# Revit family: Hager-Typ.A_SP&N_DIN_Rail_Enclosures-syst-UK-en
name_source: partatom
category: Electrical Equipment
units: mm (PartAtom-declared; Revit-internal decimal feet)

## family parameters
Cut with Voids When Loaded = No
Host = Face
Panel Configuration = Two Columns, Circuits Across
Part Type = Panelboard
Room Calculation Point = No
Round Connector Dimension = Use Diameter
Shared = No

## types (8) — shared parameters
EF000003 - Mounting method = EV000384 - Surface mounted (plaster)
EF000007 - Colour = EV000154 - Other
EF000049 - Depth = 125 mm  [stored 0.410105 ft]
EF000116 - RAL-number = 7035
EF000118 - With mounting plate = No
EF000339 - Type of cover = EV004216 - Door
EF001062 - EMC-version = No
EF001088 - Extension possible = No
EF001134 - DIN-rail = No
EF001596 - Material housing = EV000179 - Steel
EF004462 - Type of closure = EV001412 - Cylinder
EF005474 - Degree of protection (IP) = EV006410 - IP30
EF006244 - Transparent cover/door = No
EF006306 - With lock = Yes
EF015776 - Earthing terminal block = Yes
EF015777 - Neutral terminal block = Yes
EF015941 - Signal passing door = No
HG000001 - Number of columns = 1
HG000002 - With door or cover = Yes
HG000003 - Range = Type A SP&N Distribution Boards
HG000005 - Thickness = 3 mm  [stored 0.00984252 ft]
HG000006 - Flush mounted = No
HG000009 - Double swing door = No
HG000010 - Asymmetric doors = No
HG000011 - Empty rows from bottom = No
HG000017 - Distance between poles = 18 mm  [stored 0.0590551 ft]
Manufacturer = Hager
Type Comments = Type A SP&N Distribution Boards
zero-valued in all types: Default Elevation, EF000218 - Built-in depth, EF000332 - Built-in height, EF000846 - Built-in width, EF001131 - Internal depth, HG000007 - Number of empty columns, HG000008 - Number of empty rows

## per-type parameters (varying)
| type | EF000008 - Width | EF000040 - Height | EF000266 - Number of rows | EF002950 - Width in number of modular spacings | HG000004 - Manufacturer reference | Model |
| Surface mounted IP30 W254 H236 D125 8 Modular spacings - JK008 | 254 mm | 236 mm | 1 | 8 | JK008 | JK008 |
| Surface mounted IP30 W326 H236 D125 12 Modular spacings - JK012 | 326 mm | 236 mm | 1 | 12 | JK012 | JK012 |
| Surface mounted IP30 W326 H472 D125 12 Modular spacings - JK024 | 326 mm | 472 mm | 2 | 12 | JK024 | JK024 |
| Surface mounted IP30 W398 H236 D125 16 Modular spacings - JK016 | 398 mm | 236 mm | 1 | 16 | JK016 | JK016 |
| Surface mounted IP30 W398 H472 D125 16 Modular spacings - JK032 | 398 mm | 472 mm | 2 | 16 | JK032 | JK032 |
| Surface mounted IP30 W505 H236 D125 22 Modular spacings - JK022 | 505 mm  [stored 1.65682 ft] | 236 mm | 1 | 22 | JK022 | JK022 |
| Surface mounted IP30 W505 H472 D125 22 Modular spacings - JK044 | 505 mm  [stored 1.65682 ft] | 472 mm | 2 | 22 | JK044 | JK044 |
| Surface mounted IP30 W505 H708 D125 22 Modular spacings - JK066 | 505 mm  [stored 1.65682 ft] | 708 mm  [stored 2.32283 ft] | 3 | 22 | JK066 | JK066 |

note: [stored X ft] marks values corroborated as IEEE doubles in the binary element streams (Revit-internal decimal feet)

## geometry (parser evidence)
native form markers: Sweep x17
no freeform markers — native parametric forms only
